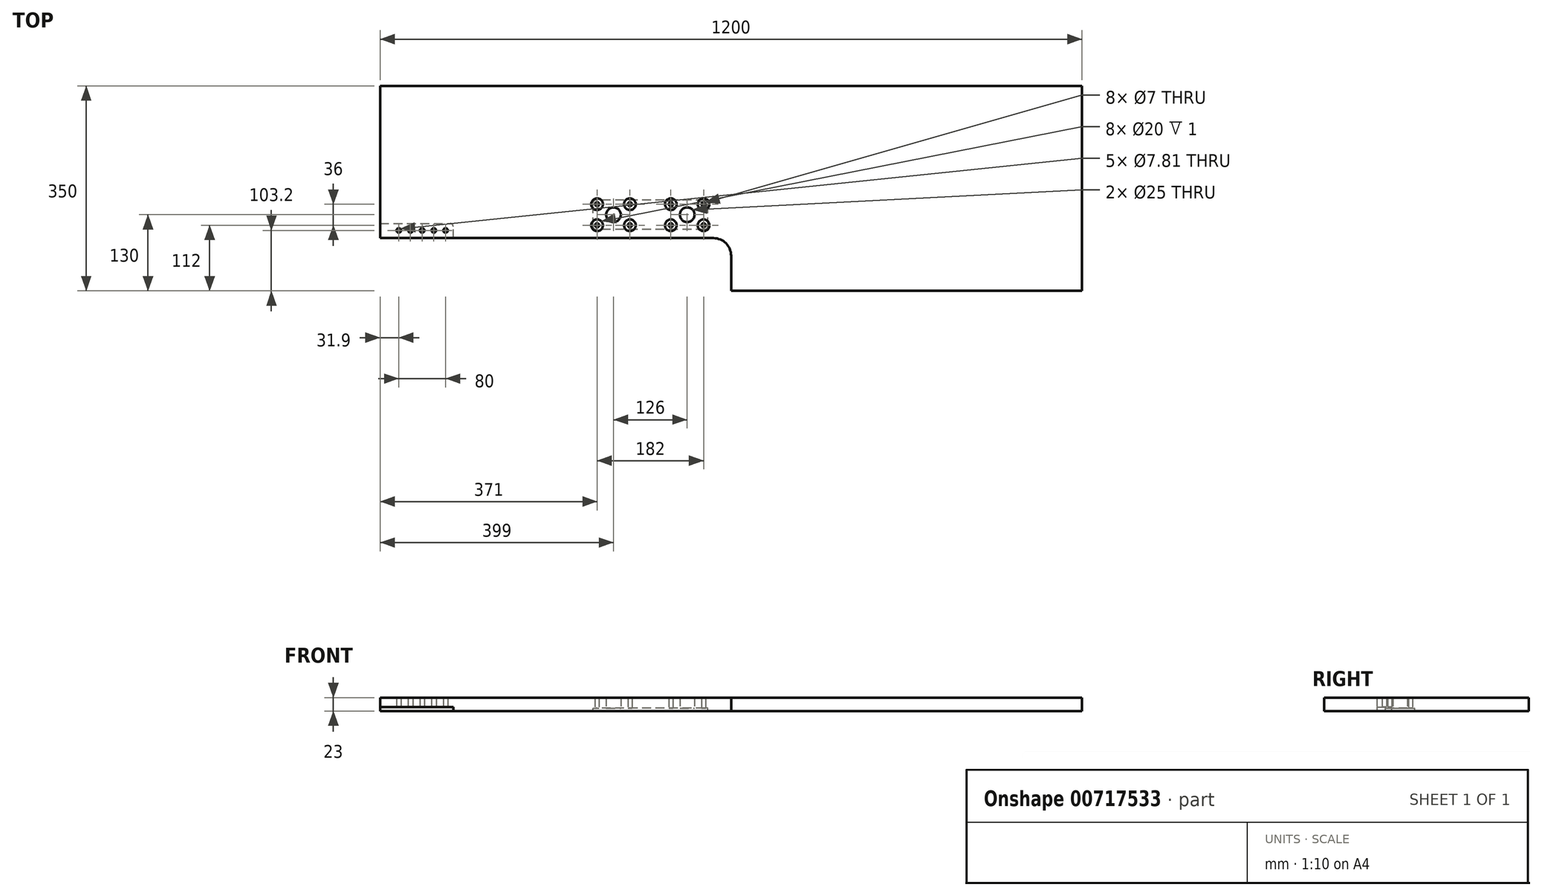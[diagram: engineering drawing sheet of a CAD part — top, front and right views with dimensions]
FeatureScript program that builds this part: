
annotation { "Feature Type Name" : "Feature", "Feature Type Description" : "" }
export const myFeature = defineFeature(function(context is Context, id is Id, definition is map)
    precondition{}
    {
        {
            var Q0;
            Q0=qCreatedBy(makeId("Top.planeOp"),FACE);
            var sketch = newSketch(context, id + "F0", { "sketchPlane" : qUnion([Q0])});
            skLineSegment(sketch, "E0.bottom", {"start": v(600, 0) * mm, "end": v(1200, 0) * mm});
            skLineSegment(sketch, "E0.top", {"start": v(0, 350) * mm, "end": v(1200, 350) * mm});
            skLineSegment(sketch, "E0.right", {"start": v(1200, 0) * mm, "end": v(1200, 350) * mm});
            skLineSegment(sketch, "E1.top", {"start": v(0, 90) * mm, "end": v(570, 90) * mm});
            skLineSegment(sketch, "E1.right", {"start": v(600, 0) * mm, "end": v(600, 60) * mm});
            skLineSegment(sketch, "E2", {"start": v(0, 90) * mm, "end": v(0, 350) * mm});
            skLineSegment(sketch, "E3", {"start": v(0, 0) * mm, "end": v(600, 0) * mm, "construction": true});
            skLineSegment(sketch, "E4", {"start": v(0, 0) * mm, "end": v(0, 90) * mm, "construction": true});
            skPoint(sketch, "E5.visualSharp", {"position": v(600, 90) * mm});
            skArc(sketch, "E5.filletArc", {"start": v(600, 60) * mm, "mid": v(591.21, 81.21) * mm, "end": v(570, 90) * mm});
            skSolve(sketch);
        }
        {
            var Q0;
            Q0 = qSketchRegion(id + "F0", true);
            var Q1;
            Q1=makeQuery(id+"F0.imprint","IMPRINT",FACE,{"disambiguationData":[TD([[makeQuery(id+"F0.imprint","IMPRINT",EDGE,{"derivedFrom":sQuery(id+"F0.wireOp",EDGE,"E0.bottom")}),1.0]])]});
            extrude(context, id + "F1", {"entities" : qUnion([Q0, Q1]), "depth" : 18 * mm, "offsetDistance" : 25 * mm});
        }
        {
            var Q0;
            Q0=makeQuery(id+"F1.opExtrude","CAP_FACE",FACE,{"disambiguationData":[OSD([sQuery(id+"F0.wireOp",EDGE,"E0.bottom"),sQuery(id+"F0.wireOp",EDGE,"E0.top"),sQuery(id+"F0.wireOp",EDGE,"E0.right"),sQuery(id+"F0.wireOp",EDGE,"E1.top"),sQuery(id+"F0.wireOp",EDGE,"E1.right"),sQuery(id+"F0.wireOp",EDGE,"E2"),sQuery(id+"F0.wireOp",EDGE,"E5.filletArc")])],"isStart":true});
            var sketch = newSketch(context, id + "F2", { "sketchPlane" : qUnion([Q0])});
            skLineSegment(sketch, "E6.bottom", {"start": v(555, -105) * mm, "end": v(369, -105) * mm});
            skLineSegment(sketch, "E6.top", {"start": v(555, -155) * mm, "end": v(369, -155) * mm});
            skLineSegment(sketch, "E6.left", {"start": v(560, -110) * mm, "end": v(560, -150) * mm});
            skLineSegment(sketch, "E6.right", {"start": v(364, -110) * mm, "end": v(364, -150) * mm});
            skPoint(sketch, "E7.visualSharp", {"position": v(560, -155) * mm});
            skArc(sketch, "E7.filletArc", {"start": v(555, -155) * mm, "mid": v(558.54, -153.54) * mm, "end": v(560, -150) * mm});
            skPoint(sketch, "E8.visualSharp", {"position": v(364, -155) * mm});
            skArc(sketch, "E8.filletArc", {"start": v(364, -150) * mm, "mid": v(365.46, -153.54) * mm, "end": v(369, -155) * mm});
            skPoint(sketch, "E9.visualSharp", {"position": v(364, -105) * mm});
            skArc(sketch, "E9.filletArc", {"start": v(369, -105) * mm, "mid": v(365.46, -106.46) * mm, "end": v(364, -110) * mm});
            skPoint(sketch, "E10.visualSharp", {"position": v(560, -105) * mm});
            skArc(sketch, "E10.filletArc", {"start": v(560, -110) * mm, "mid": v(558.54, -106.46) * mm, "end": v(555, -105) * mm});
            skSolve(sketch);
        }
        {
            var Q0;
            Q0=makeQuery(id+"F2.imprint","IMPRINT",FACE,{"disambiguationData":[TD([[makeQuery(id+"F2.imprint","IMPRINT",EDGE,{"derivedFrom":sQuery(id+"F2.wireOp",EDGE,"E6.bottom")}),-1.0]])]});
            extrude(context, id + "F3", {"entities" : qUnion([Q0]), "operationType" : NewBodyOperationType.ADD, "depth" : 5 * mm, "offsetDistance" : 25 * mm});
        }
        {
            var Q0;
            Q0=makeQuery(id+"F3.opExtrude","CAP_FACE",FACE,{"disambiguationData":[OSD([sQuery(id+"F0.wireOp",EDGE,"E0.bottom"),sQuery(id+"F0.wireOp",EDGE,"E0.top"),sQuery(id+"F0.wireOp",EDGE,"E0.right"),sQuery(id+"F0.wireOp",EDGE,"E1.top"),sQuery(id+"F0.wireOp",EDGE,"E1.right"),sQuery(id+"F0.wireOp",EDGE,"E2"),sQuery(id+"F0.wireOp",EDGE,"E5.filletArc"),sQuery(id+"F2.wireOp",EDGE,"E6.bottom"),sQuery(id+"F2.wireOp",EDGE,"E6.top"),sQuery(id+"F2.wireOp",EDGE,"E6.left"),sQuery(id+"F2.wireOp",EDGE,"E6.right")])],"isStart":false});
            var sketch = newSketch(context, id + "F4", { "sketchPlane" : qUnion([Q0])});
            skLineSegment(sketch, "E11.bottom", {"start": v(0, -90) * mm, "end": v(125, -90) * mm});
            skLineSegment(sketch, "E11.top", {"start": v(0, -114.8) * mm, "end": v(120, -114.8) * mm});
            skLineSegment(sketch, "E11.left", {"start": v(0, -90) * mm, "end": v(0, -114.8) * mm});
            skLineSegment(sketch, "E11.right", {"start": v(125, -90) * mm, "end": v(125, -109.8) * mm});
            skPoint(sketch, "E12.visualSharp", {"position": v(125, -114.8) * mm});
            skArc(sketch, "E12.filletArc", {"start": v(120, -114.8) * mm, "mid": v(123.54, -113.34) * mm, "end": v(125, -109.8) * mm});
            skSolve(sketch);
        }
        {
            var Q0;
            Q0=makeQuery(id+"F4.imprint","IMPRINT",FACE,{"disambiguationData":[TD([[makeQuery(id+"F4.imprint","IMPRINT",EDGE,{"derivedFrom":sQuery(id+"F4.wireOp",EDGE,"E11.bottom")}),-1.0]])]});
            extrude(context, id + "F5", {"entities" : qUnion([Q0]), "operationType" : NewBodyOperationType.REMOVE, "oppositeDirection" : true, "depth" : 7 * mm, "offsetDistance" : 25 * mm});
        }
        {
            var Q0;
            Q0=makeQuery(id+"F1.opExtrude","CAP_FACE",FACE,{"disambiguationData":[OSD([sQuery(id+"F0.wireOp",EDGE,"E0.bottom"),sQuery(id+"F0.wireOp",EDGE,"E0.top"),sQuery(id+"F0.wireOp",EDGE,"E0.right"),sQuery(id+"F0.wireOp",EDGE,"E1.top"),sQuery(id+"F0.wireOp",EDGE,"E1.right"),sQuery(id+"F0.wireOp",EDGE,"E2"),sQuery(id+"F0.wireOp",EDGE,"E5.filletArc")])],"isStart":true});
            var sketch = newSketch(context, id + "F6", { "sketchPlane" : qUnion([Q0])});
            skCircle(sketch, "E13", {"center": v(525, -130) * mm, "radius": 12.5 * mm});
            skCircle(sketch, "E14", {"center": v(399, -130) * mm, "radius": 12.5 * mm});
            skLineSegment(sketch, "E15", {"start": v(399, -130) * mm, "end": v(525, -130) * mm, "construction": true});
            skLineSegment(sketch, "E16.bottom", {"start": v(427, -112) * mm, "end": v(371, -112) * mm, "construction": true});
            skLineSegment(sketch, "E16.top", {"start": v(427, -148) * mm, "end": v(371, -148) * mm, "construction": true});
            skLineSegment(sketch, "E16.left", {"start": v(427, -112) * mm, "end": v(427, -148) * mm, "construction": true});
            skLineSegment(sketch, "E16.right", {"start": v(371, -112) * mm, "end": v(371, -148) * mm, "construction": true});
            skLineSegment(sketch, "E17.bottom", {"start": v(553, -112) * mm, "end": v(497, -112) * mm, "construction": true});
            skLineSegment(sketch, "E17.top", {"start": v(553, -148) * mm, "end": v(497, -148) * mm, "construction": true});
            skLineSegment(sketch, "E17.left", {"start": v(553, -112) * mm, "end": v(553, -148) * mm, "construction": true});
            skLineSegment(sketch, "E17.right", {"start": v(497, -112) * mm, "end": v(497, -148) * mm, "construction": true});
            skCircle(sketch, "E18", {"center": v(371, -112) * mm, "radius": 3.5 * mm});
            skCircle(sketch, "E19", {"center": v(427, -112) * mm, "radius": 3.5 * mm});
            skCircle(sketch, "E20", {"center": v(371, -148) * mm, "radius": 3.5 * mm});
            skCircle(sketch, "E21", {"center": v(427, -148) * mm, "radius": 3.5 * mm});
            skCircle(sketch, "E22", {"center": v(497, -148) * mm, "radius": 3.5 * mm});
            skCircle(sketch, "E23", {"center": v(497, -112) * mm, "radius": 3.5 * mm});
            skCircle(sketch, "E24", {"center": v(553, -112) * mm, "radius": 3.5 * mm});
            skCircle(sketch, "E25", {"center": v(553, -148) * mm, "radius": 3.5 * mm});
            skSolve(sketch);
        }
        {
            var Q0;
            Q0 = qSketchRegion(id + "F6", true);
            extrude(context, id + "F7", {"entities" : qUnion([Q0]), "operationType" : NewBodyOperationType.REMOVE, "oppositeDirection" : true, "depth" : 25 * mm, "offsetDistance" : 25 * mm});
        }
        {
            var Q0;
            Q0=makeQuery(id+"F1.opExtrude","CAP_FACE",FACE,{"disambiguationData":[OSD([sQuery(id+"F0.wireOp",EDGE,"E0.bottom"),sQuery(id+"F0.wireOp",EDGE,"E0.top"),sQuery(id+"F0.wireOp",EDGE,"E0.right"),sQuery(id+"F0.wireOp",EDGE,"E1.top"),sQuery(id+"F0.wireOp",EDGE,"E1.right"),sQuery(id+"F0.wireOp",EDGE,"E2"),sQuery(id+"F0.wireOp",EDGE,"E5.filletArc")])],"isStart":false});
            var sketch = newSketch(context, id + "F8", { "sketchPlane" : qUnion([Q0])});
            skCircle(sketch, "E26", {"center": v(371, 148) * mm, "radius": 10 * mm});
            skCircle(sketch, "E27", {"center": v(371, 112) * mm, "radius": 10 * mm});
            skCircle(sketch, "E28", {"center": v(427, 148) * mm, "radius": 10 * mm});
            skCircle(sketch, "E29", {"center": v(427, 112) * mm, "radius": 10 * mm});
            skCircle(sketch, "E30", {"center": v(497, 148) * mm, "radius": 10 * mm});
            skCircle(sketch, "E31", {"center": v(553, 148) * mm, "radius": 10 * mm});
            skCircle(sketch, "E32", {"center": v(553, 112) * mm, "radius": 10 * mm});
            skCircle(sketch, "E33", {"center": v(497, 112) * mm, "radius": 10 * mm});
            skSolve(sketch);
        }
        {
            var Q0;
            Q0=makeQuery(id+"F8.imprint","IMPRINT",FACE,{"disambiguationData":[TD([[makeQuery(id+"F8.imprint","IMPRINT",EDGE,{"derivedFrom":sQuery(id+"F8.wireOp",EDGE,"E26")}),1.0]])]});
            var Q1;
            Q1=makeQuery(id+"F8.imprint","IMPRINT",FACE,{"disambiguationData":[TD([[makeQuery(id+"F8.imprint","IMPRINT",EDGE,{"derivedFrom":sQuery(id+"F8.wireOp",EDGE,"E28")}),1.0]])]});
            var Q2;
            Q2=makeQuery(id+"F8.imprint","IMPRINT",FACE,{"disambiguationData":[TD([[makeQuery(id+"F8.imprint","IMPRINT",EDGE,{"derivedFrom":sQuery(id+"F8.wireOp",EDGE,"E30")}),1.0]])]});
            var Q3;
            Q3=makeQuery(id+"F8.imprint","IMPRINT",FACE,{"disambiguationData":[TD([[makeQuery(id+"F8.imprint","IMPRINT",EDGE,{"derivedFrom":sQuery(id+"F8.wireOp",EDGE,"E31")}),1.0]])]});
            var Q4;
            Q4=makeQuery(id+"F8.imprint","IMPRINT",FACE,{"disambiguationData":[TD([[makeQuery(id+"F8.imprint","IMPRINT",EDGE,{"derivedFrom":sQuery(id+"F8.wireOp",EDGE,"E32")}),1.0]])]});
            var Q5;
            Q5=makeQuery(id+"F8.imprint","IMPRINT",FACE,{"disambiguationData":[TD([[makeQuery(id+"F8.imprint","IMPRINT",EDGE,{"derivedFrom":sQuery(id+"F8.wireOp",EDGE,"E33")}),1.0]])]});
            var Q6;
            Q6=makeQuery(id+"F8.imprint","IMPRINT",FACE,{"disambiguationData":[TD([[makeQuery(id+"F8.imprint","IMPRINT",EDGE,{"derivedFrom":sQuery(id+"F8.wireOp",EDGE,"E29")}),1.0]])]});
            var Q7;
            Q7=makeQuery(id+"F8.imprint","IMPRINT",FACE,{"disambiguationData":[TD([[makeQuery(id+"F8.imprint","IMPRINT",EDGE,{"derivedFrom":sQuery(id+"F8.wireOp",EDGE,"E27")}),1.0]])]});
            extrude(context, id + "F9", {"entities" : qUnion([Q0, Q1, Q2, Q3, Q4, Q5, Q6, Q7]), "operationType" : NewBodyOperationType.REMOVE, "oppositeDirection" : true, "depth" : 1 * mm, "offsetDistance" : 25 * mm});
        }
        {
            var Q0;
            Q0=makeQuery(id+"F5.boolean.opBoolean","COPY",FACE,{"derivedFrom":makeQuery(id+"F5.opExtrude","CAP_FACE",FACE,{"disambiguationData":[OSD([sQuery(id+"F4.wireOp",EDGE,"E11.bottom"),sQuery(id+"F4.wireOp",EDGE,"E11.top"),sQuery(id+"F4.wireOp",EDGE,"E11.left"),sQuery(id+"F4.wireOp",EDGE,"E11.right"),sQuery(id+"F4.wireOp",EDGE,"E12.filletArc")])],"isStart":false})});
            var sketch = newSketch(context, id + "F10", { "sketchPlane" : qUnion([Q0])});
            skCircle(sketch, "E34", {"center": v(111.9, -103.2) * mm, "radius": 3.9 * mm});
            skCircle(sketch, "E35", {"center": v(91.9, -103.2) * mm, "radius": 3.9 * mm});
            skCircle(sketch, "E36", {"center": v(71.9, -103.2) * mm, "radius": 3.9 * mm});
            skCircle(sketch, "E37", {"center": v(51.9, -103.2) * mm, "radius": 3.9 * mm});
            skCircle(sketch, "E38", {"center": v(31.9, -103.2) * mm, "radius": 3.9 * mm});
            skLineSegment(sketch, "E39", {"start": v(111.9, -103.2) * mm, "end": v(91.9, -103.2) * mm, "construction": true});
            skLineSegment(sketch, "E40", {"start": v(91.9, -103.2) * mm, "end": v(71.9, -103.2) * mm, "construction": true});
            skLineSegment(sketch, "E41", {"start": v(71.9, -103.2) * mm, "end": v(51.9, -103.2) * mm, "construction": true});
            skLineSegment(sketch, "E42", {"start": v(51.9, -103.2) * mm, "end": v(31.9, -103.2) * mm, "construction": true});
            skSolve(sketch);
        }
        {
            var Q0;
            Q0 = qSketchRegion(id + "F10", true);
            extrude(context, id + "F11", {"entities" : qUnion([Q0]), "operationType" : NewBodyOperationType.REMOVE, "oppositeDirection" : true, "depth" : 25 * mm, "offsetDistance" : 25 * mm});
        }
    });
